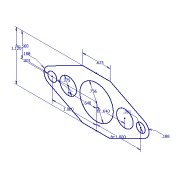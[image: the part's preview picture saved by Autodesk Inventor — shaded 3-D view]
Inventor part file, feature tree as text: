
AUTODESK INVENTOR PART (.ipt)
format: ipt  version: 2013 (Build 170138000, 138)  size: 73,216 bytes
history: native  units: in
note: dims shown in document units (in); Inventor stores cm internally (conversion verified against a paired STEP export)
features: sketch x1
ambient origin geometry x8: Origin, YZ Plane, XZ Plane, XY Plane, X Axis, Y Axis, Z Axis, Center Point
feature tree (1):
  sketch  "Sketch1"  dims[d0=0.756in d1=0.375in d2=0.64in d3=0.64in d4=0.625in d5=0.201in d6=1.0in d7=0.188in d8=1.12in d9=0.201in d10=1.0in d11=0.188in d12=0.56in]
